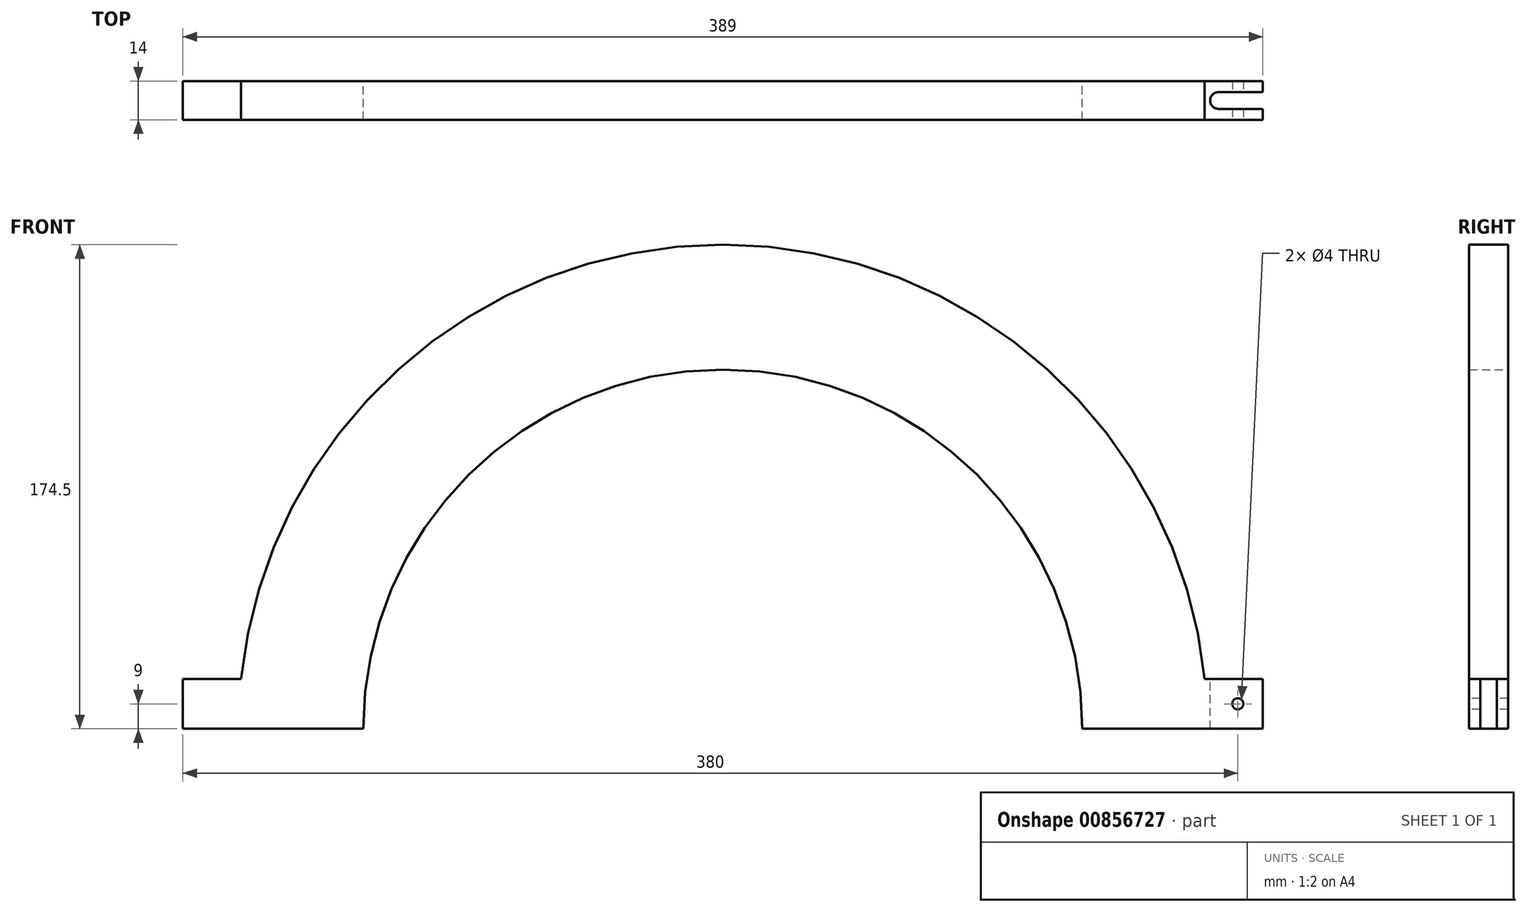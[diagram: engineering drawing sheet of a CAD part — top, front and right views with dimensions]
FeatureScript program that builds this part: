
annotation { "Feature Type Name" : "Feature", "Feature Type Description" : "" }
export const myFeature = defineFeature(function(context is Context, id is Id, definition is map)
    precondition{}
    {
        {
            var Q0;
            Q0=qCreatedBy(makeId("Front.planeOp"),FACE);
            var sketch = newSketch(context, id + "F0", { "sketchPlane" : qUnion([Q0])});
            skArc(sketch, "E0", {"start": v(174.5, 0) * mm, "mid": v(0, 174.5) * mm, "end": v(-174.5, 0) * mm});
            skArc(sketch, "E1", {"start": v(129.5, 0) * mm, "mid": v(0, 129.5) * mm, "end": v(-129.5, 0) * mm});
            skLineSegment(sketch, "E2", {"start": v(-174.5, 0) * mm, "end": v(-129.5, 0) * mm});
            skLineSegment(sketch, "E3.trimOffspring", {"start": v(129.5, 0) * mm, "end": v(174.5, 0) * mm});
            skLineSegment(sketch, "E4", {"start": v(-174.5, 0) * mm, "end": v(-174.5, -52.73) * mm, "construction": true});
            skLineSegment(sketch, "E5", {"start": v(0, 82.24) * mm, "end": v(0, -91.49) * mm, "construction": true});
            skLineSegment(sketch, "E6", {"start": v(174.5, 0) * mm, "end": v(194.5, 0) * mm});
            skLineSegment(sketch, "E7", {"start": v(194.5, 0) * mm, "end": v(194.5, 18) * mm});
            skLineSegment(sketch, "E8", {"start": v(194.5, 18) * mm, "end": v(173.57, 18) * mm});
            skLineSegment(sketch, "E9.MirrorCS", {"start": v(-194.5, 18) * mm, "end": v(-173.57, 18) * mm});
            skLineSegment(sketch, "E10.MirrorCS", {"start": v(-194.5, 0) * mm, "end": v(-194.5, 18) * mm});
            skLineSegment(sketch, "E11.MirrorCS", {"start": v(-174.5, 0) * mm, "end": v(-194.5, 0) * mm});
            skSolve(sketch);
        }
        {
            var Q0;
            Q0=qSketchRegion(id+"F0",true);
            extrude(context, id + "F1", {"entities" : qUnion([Q0]), "endBound" : BoundingType.SYMMETRIC, "depth" : 14 * mm, "offsetDistance" : 25 * mm});
        }
        {
            var Q0;
            Q0=qSketchRegion(id+"F0",true);
            extrude(context, id + "F2", {"entities" : qUnion([Q0]), "operationType" : NewBodyOperationType.ADD, "endBound" : BoundingType.SYMMETRIC, "depth" : 12 * mm, "offsetDistance" : 25 * mm});
        }
        {
            var Q0;
            Q0=makeQuery(id+"F1.opExtrude","CAP_FACE",FACE,{"disambiguationData":[OSD([sQuery(id+"F0.wireOp",EDGE,"E0"),sQuery(id+"F0.wireOp",EDGE,"E1"),sQuery(id+"F0.wireOp",EDGE,"E2"),sQuery(id+"F0.wireOp",EDGE,"E3.trimOffspring"),sQuery(id+"F0.wireOp",EDGE,"E6"),sQuery(id+"F0.wireOp",EDGE,"E7"),sQuery(id+"F0.wireOp",EDGE,"E8"),sQuery(id+"F0.wireOp",EDGE,"E9.MirrorCS"),sQuery(id+"F0.wireOp",EDGE,"E10.MirrorCS"),sQuery(id+"F0.wireOp",EDGE,"E11.MirrorCS")])],"isStart":false});
            var sketch = newSketch(context, id + "F3", { "sketchPlane" : qUnion([Q0])});
            skCircle(sketch, "E12", {"center": v(185.5, 9) * mm, "radius": 2 * mm});
            skSolve(sketch);
        }
        {
            var Q0;
            Q0 = qSketchRegion(id + "F3", true);
            extrude(context, id + "F4", {"entities" : qUnion([Q0]), "operationType" : NewBodyOperationType.REMOVE, "oppositeDirection" : true, "depth" : 25 * mm, "offsetDistance" : 25 * mm});
        }
        {
            var Q0;
            Q0=makeQuery(id+"F1.opExtrude","SWEPT_FACE",FACE,{"disambiguationData":[OSD([sQuery(id+"F0.wireOp",EDGE,"E8")])]});
            var sketch = newSketch(context, id + "F5", { "sketchPlane" : qUnion([Q0])});
            skArc(sketch, "E13", {"start": v(178.5, 3) * mm, "mid": v(175.5, 0) * mm, "end": v(178.5, -3) * mm});
            skLineSegment(sketch, "E14", {"start": v(178.5, 3) * mm, "end": v(194.5, 3) * mm});
            skLineSegment(sketch, "E15", {"start": v(178.5, -3) * mm, "end": v(194.5, -3) * mm});
            skLineSegment(sketch, "E16", {"start": v(194.5, -3) * mm, "end": v(194.5, 3) * mm});
            skSolve(sketch);
        }
        {
            var Q0;
            Q0 = qSketchRegion(id + "F5", true);
            extrude(context, id + "F6", {"entities" : qUnion([Q0]), "operationType" : NewBodyOperationType.REMOVE, "oppositeDirection" : true, "depth" : 25 * mm, "offsetDistance" : 25 * mm});
        }
    });
